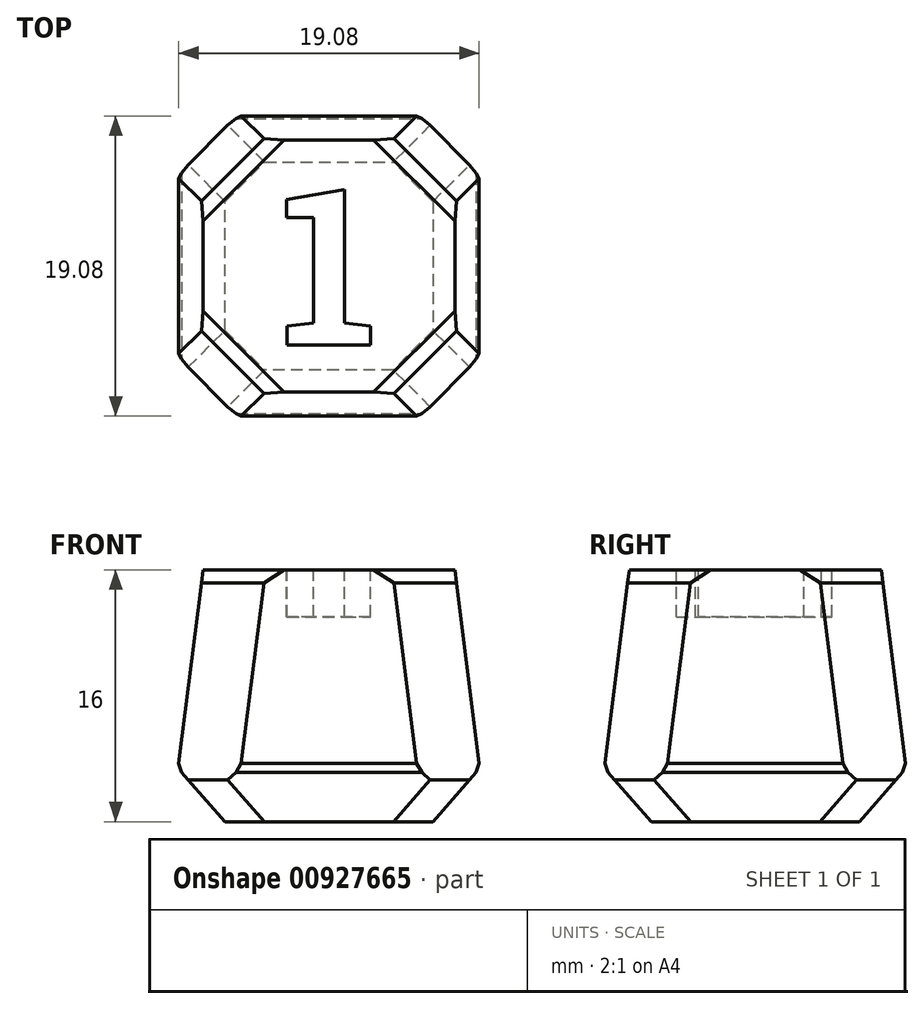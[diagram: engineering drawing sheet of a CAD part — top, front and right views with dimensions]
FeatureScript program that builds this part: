
annotation { "Feature Type Name" : "Feature", "Feature Type Description" : "" }
export const myFeature = defineFeature(function(context is Context, id is Id, definition is map)
    precondition{}
    {
        {
            var Q0;
            Q0=qCreatedBy(makeId("Top.planeOp"),FACE);
            var sketch = newSketch(context, id + "F0", { "sketchPlane" : qUnion([Q0])});
            skLineSegment(sketch, "E0.bottom", {"start": v(10, 10) * mm, "end": v(-10, 10) * mm});
            skLineSegment(sketch, "E0.top", {"start": v(10, -10) * mm, "end": v(-10, -10) * mm});
            skLineSegment(sketch, "E0.left", {"start": v(10, 10) * mm, "end": v(10, -10) * mm});
            skLineSegment(sketch, "E0.right", {"start": v(-10, 10) * mm, "end": v(-10, -10) * mm});
            skPoint(sketch, "E0.middle", {"position": v(0, 0) * mm});
            skSolve(sketch);
        }
        {
            var Q0;
            Q0 = qSketchRegion(id + "F0", true);
            extrude(context, id + "F1", {"entities" : qUnion([Q0]), "depth" : 16 * mm, "offsetDistance" : 25 * mm});
        }
        {
            var Q0;
            Q0=makeQuery(id+"F1.opExtrude","SWEPT_FACE",FACE,{"disambiguationData":[OSD([sQuery(id+"F0.wireOp",EDGE,"E0.bottom")])]});
            var sketch = newSketch(context, id + "F2", { "sketchPlane" : qUnion([Q0])});
            skLineSegment(sketch, "E1", {"start": v(-10, 16) * mm, "end": v(-8, 16) * mm});
            skLineSegment(sketch, "E2", {"start": v(-8, 16) * mm, "end": v(-10, 0) * mm});
            skLineSegment(sketch, "E3", {"start": v(10, 16) * mm, "end": v(8, 16) * mm});
            skLineSegment(sketch, "E4", {"start": v(8, 16) * mm, "end": v(10, 0) * mm});
            skLineSegment(sketch, "E5", {"start": v(10, 0) * mm, "end": v(10, 16) * mm});
            skLineSegment(sketch, "E6", {"start": v(-10, 16) * mm, "end": v(-10, 0) * mm});
            skSolve(sketch);
        }
        {
            var Q0;
            Q0=makeQuery(id+"F1.opExtrude","SWEPT_FACE",FACE,{"disambiguationData":[OSD([sQuery(id+"F0.wireOp",EDGE,"E0.right")])]});
            var sketch = newSketch(context, id + "F3", { "sketchPlane" : qUnion([Q0])});
            skLineSegment(sketch, "E7", {"start": v(-10, 16) * mm, "end": v(-8, 16) * mm});
            skLineSegment(sketch, "E8", {"start": v(-8, 16) * mm, "end": v(-10, 0) * mm});
            skLineSegment(sketch, "E9", {"start": v(-10, 0) * mm, "end": v(-10, 16) * mm});
            skLineSegment(sketch, "E10", {"start": v(10, 16) * mm, "end": v(8, 16) * mm});
            skLineSegment(sketch, "E11", {"start": v(8, 16) * mm, "end": v(10, 0) * mm});
            skLineSegment(sketch, "E12", {"start": v(10, 0) * mm, "end": v(10, 16) * mm});
            skSolve(sketch);
        }
        {
            var Q0;
            Q0=makeQuery(id+"F3.imprint","IMPRINT",FACE,{"disambiguationData":[TD([[makeQuery(id+"F3.imprint","IMPRINT",EDGE,{"derivedFrom":sQuery(id+"F3.wireOp",EDGE,"E7")}),-1.0]])]});
            var Q1;
            Q1=makeQuery(id+"F3.imprint","IMPRINT",FACE,{"disambiguationData":[TD([[makeQuery(id+"F3.imprint","IMPRINT",EDGE,{"derivedFrom":sQuery(id+"F3.wireOp",EDGE,"E10")}),-1.0]])]});
            extrude(context, id + "F4", {"entities" : qUnion([Q0, Q1]), "operationType" : NewBodyOperationType.REMOVE, "oppositeDirection" : true, "depth" : 25 * mm, "offsetDistance" : 25 * mm});
        }
        {
            var Q0;
            Q0=makeQuery(id+"F2.imprint","IMPRINT",FACE,{"disambiguationData":[TD([[makeQuery(id+"F2.imprint","IMPRINT",EDGE,{"derivedFrom":sQuery(id+"F2.wireOp",EDGE,"E1")}),-1.0]])]});
            var Q1;
            Q1=makeQuery(id+"F2.imprint","IMPRINT",FACE,{"disambiguationData":[TD([[makeQuery(id+"F2.imprint","IMPRINT",EDGE,{"derivedFrom":sQuery(id+"F2.wireOp",EDGE,"E3")}),-1.0]])]});
            extrude(context, id + "F5", {"entities" : qUnion([Q0, Q1]), "operationType" : NewBodyOperationType.REMOVE, "oppositeDirection" : true, "depth" : 25 * mm, "offsetDistance" : 25 * mm});
        }
        {
            var Q0;
            Q0=makeQuery(id+"F1.opExtrude","CAP_FACE",FACE,{"disambiguationData":[OSD([sQuery(id+"F0.wireOp",EDGE,"E0.bottom"),sQuery(id+"F0.wireOp",EDGE,"E0.top"),sQuery(id+"F0.wireOp",EDGE,"E0.left"),sQuery(id+"F0.wireOp",EDGE,"E0.right")])],"isStart":false});
            var sketch = newSketch(context, id + "F6", { "sketchPlane" : qUnion([Q0])});
            skText(sketch, "E13", { "text": "1", "fontName": "RobotoSlab-Bold.ttf"});
            skLineSegment(sketch, "E14", {"start": v(8, 0) * mm, "end": v(4.46, 0) * mm});
            skLineSegment(sketch, "E15", {"start": v(-3.1, 0) * mm, "end": v(3.5, 0) * mm, "construction": true});
            skLineSegment(sketch, "E16", {"start": v(0.2, 5.58) * mm, "end": v(0.2, 5) * mm, "construction": true});
            skLineSegment(sketch, "E17", {"start": v(3.5, 0) * mm, "end": v(4.46, 0) * mm, "construction": true});
            skLineSegment(sketch, "E18", {"start": v(3.5, -5) * mm, "end": v(0.2, -5) * mm, "construction": true});
            const initialGuessF6  = {"E13": [-0.0031, -0.005, 1, 0, 0.01]};
            skSetInitialGuess(sketch, initialGuessF6);
            skSolve(sketch);
        }
        {
            var Q0;
            Q0=makeQuery(id+"F6.imprint","IMPRINT",FACE,{"disambiguationData":[TD([[makeQuery(id+"F6.imprint","IMPRINT",EDGE,{"derivedFrom":sQuery(id+"F6.wireOp",EDGE,"E13.sketch_text.stroke-0")}),-1.0]])]});
            extrude(context, id + "F7", {"entities" : qUnion([Q0]), "operationType" : NewBodyOperationType.REMOVE, "oppositeDirection" : true, "depth" : 3 * mm, "offsetDistance" : 25 * mm});
        }
        {
            var Q0;
            Q0=makeQuery(id+"F1.opExtrude","CAP_FACE",FACE,{"disambiguationData":[OSD([sQuery(id+"F0.wireOp",EDGE,"E0.bottom"),sQuery(id+"F0.wireOp",EDGE,"E0.top"),sQuery(id+"F0.wireOp",EDGE,"E0.left"),sQuery(id+"F0.wireOp",EDGE,"E0.right")])],"isStart":true});
            chamfer(context, id + "F8", {"entities" : qUnion([Q0]), "width" : 3 * mm, "tangentPropagation" : true});
        }
        {
            var Q0;
            Q0=makeQuery(id+"F5.boolean.opBoolean","INTERSECT",EDGE,{"derivedFrom":[makeQuery(id+"F4.boolean.opBoolean","COPY",FACE,{"derivedFrom":makeQuery(id+"F4.opExtrude","SWEPT_FACE",FACE,{"disambiguationData":[OSD([sQuery(id+"F3.wireOp",EDGE,"E11")])]})}),makeQuery(id+"F5.opExtrude","SWEPT_FACE",FACE,{"disambiguationData":[OSD([sQuery(id+"F2.wireOp",EDGE,"E4")])]})]});
            var Q1;
            Q1=makeQuery(id+"F5.boolean.opBoolean","INTERSECT",EDGE,{"derivedFrom":[makeQuery(id+"F4.boolean.opBoolean","COPY",FACE,{"derivedFrom":makeQuery(id+"F4.opExtrude","SWEPT_FACE",FACE,{"disambiguationData":[OSD([sQuery(id+"F3.wireOp",EDGE,"E11")])]})}),makeQuery(id+"F5.opExtrude","SWEPT_FACE",FACE,{"disambiguationData":[OSD([sQuery(id+"F2.wireOp",EDGE,"E2")])]})]});
            var Q2;
            Q2=makeQuery(id+"F5.boolean.opBoolean","INTERSECT",EDGE,{"derivedFrom":[makeQuery(id+"F4.boolean.opBoolean","COPY",FACE,{"derivedFrom":makeQuery(id+"F4.opExtrude","SWEPT_FACE",FACE,{"disambiguationData":[OSD([sQuery(id+"F3.wireOp",EDGE,"E8")])]})}),makeQuery(id+"F5.opExtrude","SWEPT_FACE",FACE,{"disambiguationData":[OSD([sQuery(id+"F2.wireOp",EDGE,"E2")])]})]});
            var Q3;
            Q3=makeQuery(id+"F5.boolean.opBoolean","INTERSECT",EDGE,{"derivedFrom":[makeQuery(id+"F4.boolean.opBoolean","COPY",FACE,{"derivedFrom":makeQuery(id+"F4.opExtrude","SWEPT_FACE",FACE,{"disambiguationData":[OSD([sQuery(id+"F3.wireOp",EDGE,"E8")])]})}),makeQuery(id+"F5.opExtrude","SWEPT_FACE",FACE,{"disambiguationData":[OSD([sQuery(id+"F2.wireOp",EDGE,"E4")])]})]});
            chamfer(context, id + "F9", {"entities" : qUnion([Q0, Q1, Q2, Q3]), "width" : 4 * mm, "tangentPropagation" : true});
        }
        {
            var Q0;
            Q0=makeQuery(id+"F8.opChamfer","BLEND_EDGE",EDGE,{"blendedFrom":[makeQuery(id+"F4.boolean.opBoolean","MERGE",EDGE,{"derivedFrom":[makeQuery(id+"F1.opExtrude","CAP_EDGE",EDGE,{"disambiguationData":[OSD([sQuery(id+"F0.wireOp",EDGE,"E0.top")])],"isStart":true})],"fromTools":[makeQuery(id+"F4.opExtrude","SWEPT_EDGE",EDGE,{"disambiguationData":[OSD([sQuery(id+"F0.wireOp",EDGE,"E0.right"),sQuery(id+"F3.wireOp",EDGE,"E11"),sQuery(id+"F3.wireOp",EDGE,"E12")])]})]}),makeQuery(id+"F5.boolean.opBoolean","MERGE",EDGE,{"derivedFrom":[makeQuery(id+"F1.opExtrude","CAP_EDGE",EDGE,{"disambiguationData":[OSD([sQuery(id+"F0.wireOp",EDGE,"E0.left")])],"isStart":true})],"fromTools":[makeQuery(id+"F5.opExtrude","SWEPT_EDGE",EDGE,{"disambiguationData":[OSD([sQuery(id+"F0.wireOp",EDGE,"E0.bottom"),sQuery(id+"F2.wireOp",EDGE,"E2"),sQuery(id+"F2.wireOp",EDGE,"E6")])]})]})],"blendedInto":[]});
            var Q1;
            {var subQ0=sQuery(id+"F0.wireOp",EDGE,"E0.bottom");Q1=makeQuery(id+"F8.opChamfer","BLEND_EDGE",EDGE,{"blendedFrom":[makeQuery(id+"F4.boolean.opBoolean","MERGE",EDGE,{"derivedFrom":[makeQuery(id+"F1.opExtrude","CAP_EDGE",EDGE,{"disambiguationData":[OSD([subQ0])],"isStart":true})],"fromTools":[makeQuery(id+"F4.opExtrude","SWEPT_EDGE",EDGE,{"disambiguationData":[OSD([sQuery(id+"F0.wireOp",EDGE,"E0.right"),sQuery(id+"F3.wireOp",EDGE,"E8"),sQuery(id+"F3.wireOp",EDGE,"E9")])]})]}),makeQuery(id+"F5.boolean.opBoolean","MERGE",EDGE,{"derivedFrom":[makeQuery(id+"F1.opExtrude","CAP_EDGE",EDGE,{"disambiguationData":[OSD([sQuery(id+"F0.wireOp",EDGE,"E0.left")])],"isStart":true})],"fromTools":[makeQuery(id+"F5.opExtrude","SWEPT_EDGE",EDGE,{"disambiguationData":[OSD([subQ0,sQuery(id+"F2.wireOp",EDGE,"E2"),sQuery(id+"F2.wireOp",EDGE,"E6")])]})]})],"blendedInto":[]});}
            var Q2;
            {var subQ0=sQuery(id+"F0.wireOp",EDGE,"E0.bottom");var subQ1=sQuery(id+"F0.wireOp",EDGE,"E0.right");Q2=makeQuery(id+"F8.opChamfer","BLEND_EDGE",EDGE,{"blendedFrom":[makeQuery(id+"F4.boolean.opBoolean","MERGE",EDGE,{"derivedFrom":[makeQuery(id+"F1.opExtrude","CAP_EDGE",EDGE,{"disambiguationData":[OSD([subQ0])],"isStart":true})],"fromTools":[makeQuery(id+"F4.opExtrude","SWEPT_EDGE",EDGE,{"disambiguationData":[OSD([subQ1,sQuery(id+"F3.wireOp",EDGE,"E8"),sQuery(id+"F3.wireOp",EDGE,"E9")])]})]}),makeQuery(id+"F5.boolean.opBoolean","MERGE",EDGE,{"derivedFrom":[makeQuery(id+"F1.opExtrude","CAP_EDGE",EDGE,{"disambiguationData":[OSD([subQ1])],"isStart":true})],"fromTools":[makeQuery(id+"F5.opExtrude","SWEPT_EDGE",EDGE,{"disambiguationData":[OSD([subQ0,sQuery(id+"F2.wireOp",EDGE,"E4"),sQuery(id+"F2.wireOp",EDGE,"E5")])]})]})],"blendedInto":[]});}
            var Q3;
            {var subQ0=sQuery(id+"F0.wireOp",EDGE,"E0.right");Q3=makeQuery(id+"F8.opChamfer","BLEND_EDGE",EDGE,{"blendedFrom":[makeQuery(id+"F4.boolean.opBoolean","MERGE",EDGE,{"derivedFrom":[makeQuery(id+"F1.opExtrude","CAP_EDGE",EDGE,{"disambiguationData":[OSD([sQuery(id+"F0.wireOp",EDGE,"E0.top")])],"isStart":true})],"fromTools":[makeQuery(id+"F4.opExtrude","SWEPT_EDGE",EDGE,{"disambiguationData":[OSD([subQ0,sQuery(id+"F3.wireOp",EDGE,"E11"),sQuery(id+"F3.wireOp",EDGE,"E12")])]})]}),makeQuery(id+"F5.boolean.opBoolean","MERGE",EDGE,{"derivedFrom":[makeQuery(id+"F1.opExtrude","CAP_EDGE",EDGE,{"disambiguationData":[OSD([subQ0])],"isStart":true})],"fromTools":[makeQuery(id+"F5.opExtrude","SWEPT_EDGE",EDGE,{"disambiguationData":[OSD([sQuery(id+"F0.wireOp",EDGE,"E0.bottom"),sQuery(id+"F2.wireOp",EDGE,"E4"),sQuery(id+"F2.wireOp",EDGE,"E5")])]})]})],"blendedInto":[]});}
            chamfer(context, id + "F10", {"entities" : qUnion([Q0, Q1, Q2, Q3]), "width" : 3.35 * mm, "tangentPropagation" : true});
        }
        {
            var Q0;
            {var subQ0=sQuery(id+"F3.wireOp",EDGE,"E8");Q0=makeQuery(id+"F8.opChamfer","BLEND_EDGE",EDGE,{"blendedFrom":[makeQuery(id+"F4.boolean.opBoolean","MERGE",EDGE,{"derivedFrom":[makeQuery(id+"F1.opExtrude","CAP_EDGE",EDGE,{"disambiguationData":[OSD([sQuery(id+"F0.wireOp",EDGE,"E0.bottom")])],"isStart":true})],"fromTools":[makeQuery(id+"F4.opExtrude","SWEPT_EDGE",EDGE,{"disambiguationData":[OSD([sQuery(id+"F0.wireOp",EDGE,"E0.right"),subQ0,sQuery(id+"F3.wireOp",EDGE,"E9")])]})]}),makeQuery(id+"F4.boolean.opBoolean","COPY",FACE,{"derivedFrom":makeQuery(id+"F4.opExtrude","SWEPT_FACE",FACE,{"disambiguationData":[OSD([subQ0])]})})],"blendedInto":[makeQuery(id+"F4.boolean.opBoolean","COPY",FACE,{"derivedFrom":makeQuery(id+"F4.opExtrude","SWEPT_FACE",FACE,{"disambiguationData":[OSD([subQ0])]})})]});}
            var Q1;
            {var subQ0=sQuery(id+"F2.wireOp",EDGE,"E4");Q1=makeQuery(id+"F8.opChamfer","BLEND_EDGE",EDGE,{"blendedFrom":[makeQuery(id+"F5.boolean.opBoolean","MERGE",EDGE,{"derivedFrom":[makeQuery(id+"F1.opExtrude","CAP_EDGE",EDGE,{"disambiguationData":[OSD([sQuery(id+"F0.wireOp",EDGE,"E0.right")])],"isStart":true})],"fromTools":[makeQuery(id+"F5.opExtrude","SWEPT_EDGE",EDGE,{"disambiguationData":[OSD([sQuery(id+"F0.wireOp",EDGE,"E0.bottom"),subQ0,sQuery(id+"F2.wireOp",EDGE,"E5")])]})]}),makeQuery(id+"F5.boolean.opBoolean","COPY",FACE,{"derivedFrom":makeQuery(id+"F5.opExtrude","SWEPT_FACE",FACE,{"disambiguationData":[OSD([subQ0])]})})],"blendedInto":[makeQuery(id+"F5.boolean.opBoolean","COPY",FACE,{"derivedFrom":makeQuery(id+"F5.opExtrude","SWEPT_FACE",FACE,{"disambiguationData":[OSD([subQ0])]})})]});}
            var Q2;
            {var subQ0=sQuery(id+"F3.wireOp",EDGE,"E11");Q2=makeQuery(id+"F8.opChamfer","BLEND_EDGE",EDGE,{"blendedFrom":[makeQuery(id+"F4.boolean.opBoolean","MERGE",EDGE,{"derivedFrom":[makeQuery(id+"F1.opExtrude","CAP_EDGE",EDGE,{"disambiguationData":[OSD([sQuery(id+"F0.wireOp",EDGE,"E0.top")])],"isStart":true})],"fromTools":[makeQuery(id+"F4.opExtrude","SWEPT_EDGE",EDGE,{"disambiguationData":[OSD([sQuery(id+"F0.wireOp",EDGE,"E0.right"),subQ0,sQuery(id+"F3.wireOp",EDGE,"E12")])]})]}),makeQuery(id+"F4.boolean.opBoolean","COPY",FACE,{"derivedFrom":makeQuery(id+"F4.opExtrude","SWEPT_FACE",FACE,{"disambiguationData":[OSD([subQ0])]})})],"blendedInto":[makeQuery(id+"F4.boolean.opBoolean","COPY",FACE,{"derivedFrom":makeQuery(id+"F4.opExtrude","SWEPT_FACE",FACE,{"disambiguationData":[OSD([subQ0])]})})]});}
            var Q3;
            {var subQ0=sQuery(id+"F2.wireOp",EDGE,"E2");Q3=makeQuery(id+"F8.opChamfer","BLEND_EDGE",EDGE,{"blendedFrom":[makeQuery(id+"F5.boolean.opBoolean","MERGE",EDGE,{"derivedFrom":[makeQuery(id+"F1.opExtrude","CAP_EDGE",EDGE,{"disambiguationData":[OSD([sQuery(id+"F0.wireOp",EDGE,"E0.left")])],"isStart":true})],"fromTools":[makeQuery(id+"F5.opExtrude","SWEPT_EDGE",EDGE,{"disambiguationData":[OSD([sQuery(id+"F0.wireOp",EDGE,"E0.bottom"),subQ0,sQuery(id+"F2.wireOp",EDGE,"E6")])]})]}),makeQuery(id+"F5.boolean.opBoolean","COPY",FACE,{"derivedFrom":makeQuery(id+"F5.opExtrude","SWEPT_FACE",FACE,{"disambiguationData":[OSD([subQ0])]})})],"blendedInto":[makeQuery(id+"F5.boolean.opBoolean","COPY",FACE,{"derivedFrom":makeQuery(id+"F5.opExtrude","SWEPT_FACE",FACE,{"disambiguationData":[OSD([subQ0])]})})]});}
            chamfer(context, id + "F11", {"entities" : qUnion([Q0, Q1, Q2, Q3]), "width" : .75 * mm, "tangentPropagation" : true});
        }
        {
            var Q0;
            Q0=makeQuery(id+"F4.boolean.opBoolean","COPY",EDGE,{"derivedFrom":makeQuery(id+"F4.opExtrude","SWEPT_EDGE",EDGE,{"disambiguationData":[OSD([sQuery(id+"F0.wireOp",EDGE,"E0.right"),sQuery(id+"F3.wireOp",EDGE,"E7"),sQuery(id+"F3.wireOp",EDGE,"E8")])]})});
            var Q1;
            Q1=makeQuery(id+"F9.opChamfer","BLEND_EDGE",EDGE,{"blendedFrom":[makeQuery(id+"F5.boolean.opBoolean","INTERSECT",EDGE,{"derivedFrom":[makeQuery(id+"F4.boolean.opBoolean","COPY",FACE,{"derivedFrom":makeQuery(id+"F4.opExtrude","SWEPT_FACE",FACE,{"disambiguationData":[OSD([sQuery(id+"F3.wireOp",EDGE,"E8")])]})}),makeQuery(id+"F5.opExtrude","SWEPT_FACE",FACE,{"disambiguationData":[OSD([sQuery(id+"F2.wireOp",EDGE,"E2")])]})]}),makeQuery(id+"F1.opExtrude","CAP_FACE",FACE,{"disambiguationData":[OSD([sQuery(id+"F0.wireOp",EDGE,"E0.bottom"),sQuery(id+"F0.wireOp",EDGE,"E0.top"),sQuery(id+"F0.wireOp",EDGE,"E0.left"),sQuery(id+"F0.wireOp",EDGE,"E0.right")])],"isStart":false})],"blendedInto":[makeQuery(id+"F1.opExtrude","CAP_FACE",FACE,{"disambiguationData":[OSD([sQuery(id+"F0.wireOp",EDGE,"E0.bottom"),sQuery(id+"F0.wireOp",EDGE,"E0.top"),sQuery(id+"F0.wireOp",EDGE,"E0.left"),sQuery(id+"F0.wireOp",EDGE,"E0.right")])],"isStart":false})]});
            var Q2;
            Q2=makeQuery(id+"F5.boolean.opBoolean","COPY",EDGE,{"derivedFrom":makeQuery(id+"F5.opExtrude","SWEPT_EDGE",EDGE,{"disambiguationData":[OSD([sQuery(id+"F0.wireOp",EDGE,"E0.bottom"),sQuery(id+"F2.wireOp",EDGE,"E1"),sQuery(id+"F2.wireOp",EDGE,"E2")])]})});
            var Q3;
            Q3=makeQuery(id+"F9.opChamfer","BLEND_EDGE",EDGE,{"blendedFrom":[makeQuery(id+"F5.boolean.opBoolean","INTERSECT",EDGE,{"derivedFrom":[makeQuery(id+"F4.boolean.opBoolean","COPY",FACE,{"derivedFrom":makeQuery(id+"F4.opExtrude","SWEPT_FACE",FACE,{"disambiguationData":[OSD([sQuery(id+"F3.wireOp",EDGE,"E11")])]})}),makeQuery(id+"F5.opExtrude","SWEPT_FACE",FACE,{"disambiguationData":[OSD([sQuery(id+"F2.wireOp",EDGE,"E2")])]})]}),makeQuery(id+"F1.opExtrude","CAP_FACE",FACE,{"disambiguationData":[OSD([sQuery(id+"F0.wireOp",EDGE,"E0.bottom"),sQuery(id+"F0.wireOp",EDGE,"E0.top"),sQuery(id+"F0.wireOp",EDGE,"E0.left"),sQuery(id+"F0.wireOp",EDGE,"E0.right")])],"isStart":false})],"blendedInto":[makeQuery(id+"F1.opExtrude","CAP_FACE",FACE,{"disambiguationData":[OSD([sQuery(id+"F0.wireOp",EDGE,"E0.bottom"),sQuery(id+"F0.wireOp",EDGE,"E0.top"),sQuery(id+"F0.wireOp",EDGE,"E0.left"),sQuery(id+"F0.wireOp",EDGE,"E0.right")])],"isStart":false})]});
            var Q4;
            Q4=makeQuery(id+"F4.boolean.opBoolean","COPY",EDGE,{"derivedFrom":makeQuery(id+"F4.opExtrude","SWEPT_EDGE",EDGE,{"disambiguationData":[OSD([sQuery(id+"F0.wireOp",EDGE,"E0.right"),sQuery(id+"F3.wireOp",EDGE,"E10"),sQuery(id+"F3.wireOp",EDGE,"E11")])]})});
            var Q5;
            Q5=makeQuery(id+"F9.opChamfer","BLEND_EDGE",EDGE,{"blendedFrom":[makeQuery(id+"F5.boolean.opBoolean","INTERSECT",EDGE,{"derivedFrom":[makeQuery(id+"F4.boolean.opBoolean","COPY",FACE,{"derivedFrom":makeQuery(id+"F4.opExtrude","SWEPT_FACE",FACE,{"disambiguationData":[OSD([sQuery(id+"F3.wireOp",EDGE,"E11")])]})}),makeQuery(id+"F5.opExtrude","SWEPT_FACE",FACE,{"disambiguationData":[OSD([sQuery(id+"F2.wireOp",EDGE,"E4")])]})]}),makeQuery(id+"F1.opExtrude","CAP_FACE",FACE,{"disambiguationData":[OSD([sQuery(id+"F0.wireOp",EDGE,"E0.bottom"),sQuery(id+"F0.wireOp",EDGE,"E0.top"),sQuery(id+"F0.wireOp",EDGE,"E0.left"),sQuery(id+"F0.wireOp",EDGE,"E0.right")])],"isStart":false})],"blendedInto":[makeQuery(id+"F1.opExtrude","CAP_FACE",FACE,{"disambiguationData":[OSD([sQuery(id+"F0.wireOp",EDGE,"E0.bottom"),sQuery(id+"F0.wireOp",EDGE,"E0.top"),sQuery(id+"F0.wireOp",EDGE,"E0.left"),sQuery(id+"F0.wireOp",EDGE,"E0.right")])],"isStart":false})]});
            var Q6;
            Q6=makeQuery(id+"F5.boolean.opBoolean","COPY",EDGE,{"derivedFrom":makeQuery(id+"F5.opExtrude","SWEPT_EDGE",EDGE,{"disambiguationData":[OSD([sQuery(id+"F0.wireOp",EDGE,"E0.bottom"),sQuery(id+"F2.wireOp",EDGE,"E3"),sQuery(id+"F2.wireOp",EDGE,"E4")])]})});
            var Q7;
            Q7=makeQuery(id+"F9.opChamfer","BLEND_EDGE",EDGE,{"blendedFrom":[makeQuery(id+"F5.boolean.opBoolean","INTERSECT",EDGE,{"derivedFrom":[makeQuery(id+"F4.boolean.opBoolean","COPY",FACE,{"derivedFrom":makeQuery(id+"F4.opExtrude","SWEPT_FACE",FACE,{"disambiguationData":[OSD([sQuery(id+"F3.wireOp",EDGE,"E8")])]})}),makeQuery(id+"F5.opExtrude","SWEPT_FACE",FACE,{"disambiguationData":[OSD([sQuery(id+"F2.wireOp",EDGE,"E4")])]})]}),makeQuery(id+"F1.opExtrude","CAP_FACE",FACE,{"disambiguationData":[OSD([sQuery(id+"F0.wireOp",EDGE,"E0.bottom"),sQuery(id+"F0.wireOp",EDGE,"E0.top"),sQuery(id+"F0.wireOp",EDGE,"E0.left"),sQuery(id+"F0.wireOp",EDGE,"E0.right")])],"isStart":false})],"blendedInto":[makeQuery(id+"F1.opExtrude","CAP_FACE",FACE,{"disambiguationData":[OSD([sQuery(id+"F0.wireOp",EDGE,"E0.bottom"),sQuery(id+"F0.wireOp",EDGE,"E0.top"),sQuery(id+"F0.wireOp",EDGE,"E0.left"),sQuery(id+"F0.wireOp",EDGE,"E0.right")])],"isStart":false})]});
            chamfer(context, id + "F12", {"entities" : qUnion([Q0, Q1, Q2, Q3, Q4, Q5, Q6, Q7]), "width" : 1 * mm, "tangentPropagation" : true});
        }
    });
